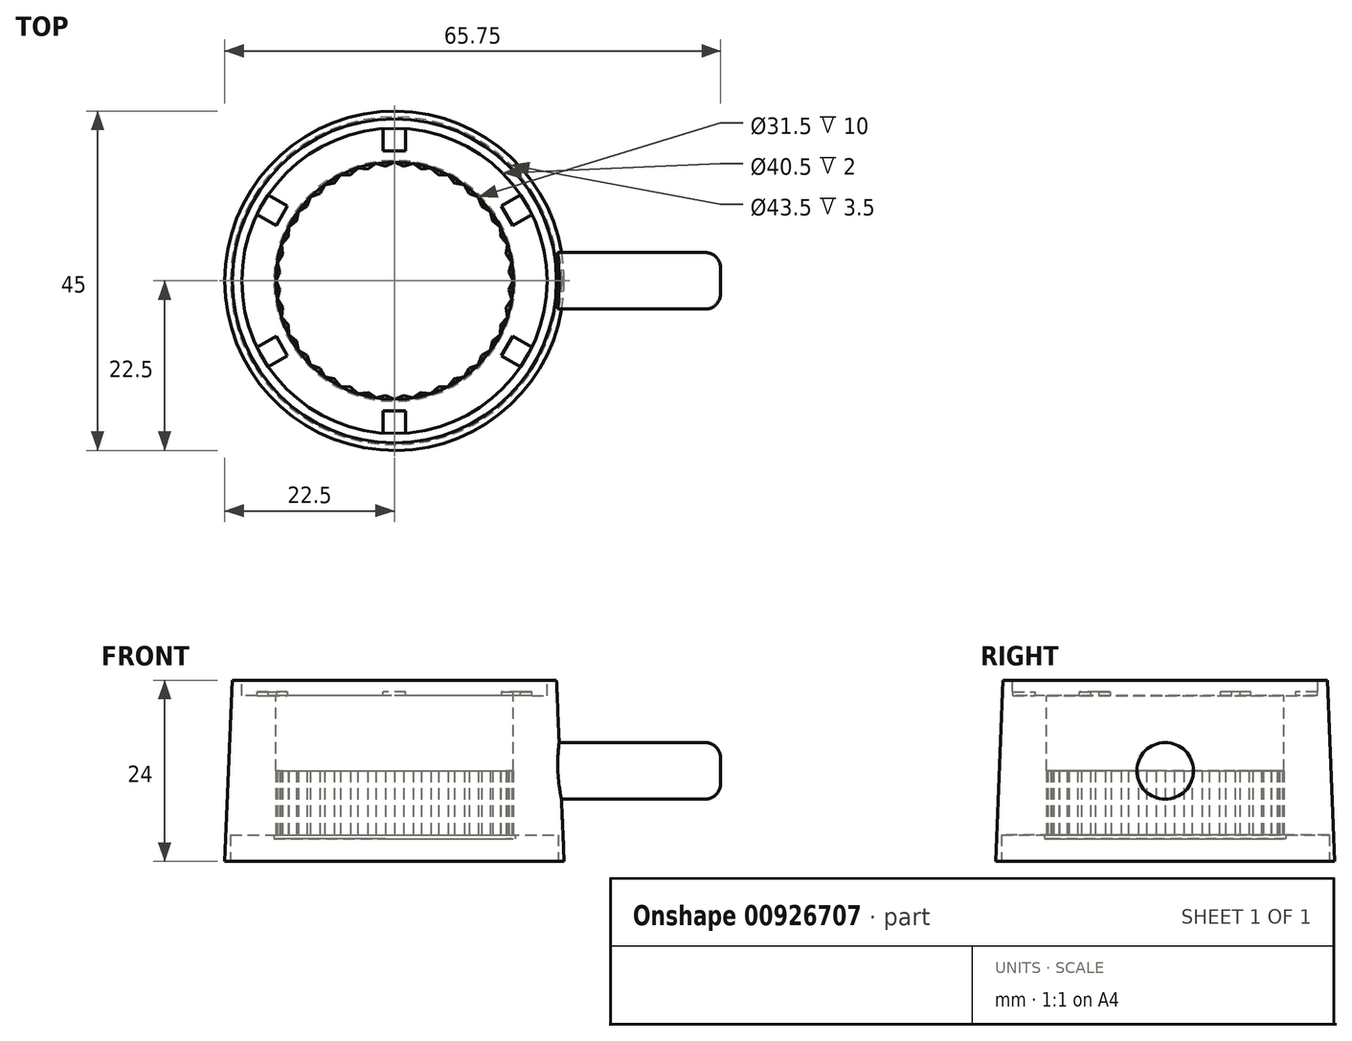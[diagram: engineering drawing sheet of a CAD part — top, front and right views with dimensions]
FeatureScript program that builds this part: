
annotation { "Feature Type Name" : "Feature", "Feature Type Description" : "" }
export const myFeature = defineFeature(function(context is Context, id is Id, definition is map)
    precondition{}
    {
        {
            var Q0;
            Q0=qCreatedBy(makeId("Top.planeOp"),FACE);
            var sketch = newSketch(context, id + "F0", { "sketchPlane" : qUnion([Q0])});
            skCircle(sketch, "E0", {"center": v(0, 0) * mm, "radius": 22.5 * mm});
            skSolve(sketch);
        }
        {
            var Q0;
            Q0=qCreatedBy(makeId("Top.planeOp"),FACE);
            cPlane(context, id + "F1", {"entities" : qUnion([Q0]), "cplaneType" : CPlaneType.OFFSET, "offset" : 24 * mm, "width" : 150 * mm, "height" : 150 * mm});
        }
        {
            var Q0;
            Q0=qCreatedBy(id+"F1.planeOp",FACE);
            var sketch = newSketch(context, id + "F2", { "sketchPlane" : qUnion([Q0])});
            skCircle(sketch, "E1", {"center": v(0, 0) * mm, "radius": 21.5 * mm});
            skSolve(sketch);
        }
        {
            var Q0;
            Q0=makeQuery(id+"F0.imprint","IMPRINT",FACE,{"disambiguationData":[TD([[makeQuery(id+"F0.imprint","IMPRINT",EDGE,{"derivedFrom":sQuery(id+"F0.wireOp",EDGE,"E0")}),1.0]])]});
            var Q1;
            Q1=makeQuery(id+"F2.imprint","IMPRINT",FACE,{"disambiguationData":[TD([[makeQuery(id+"F2.imprint","IMPRINT",EDGE,{"derivedFrom":sQuery(id+"F2.wireOp",EDGE,"E1")}),1.0]])]});
            loft(context, id + "F3", {"sheetProfilesArray" : [{ "sheetProfileEntities" : qUnion([Q0]) }, { "sheetProfileEntities" : qUnion([Q1]) }]});
        }
        {
            var Q0;
            Q0=makeQuery(id+"F3.opLoft","CAP_FACE",FACE,{"disambiguationData":[OSD([makeQuery(id+"F2.imprint","IMPRINT",FACE,{"disambiguationData":[TD([[makeQuery(id+"F2.imprint","IMPRINT",EDGE,{"derivedFrom":sQuery(id+"F2.wireOp",EDGE,"E1")}),1.0]])]})])],"isStart":true});
            var sketch = newSketch(context, id + "F4", { "sketchPlane" : qUnion([Q0])});
            skCircle(sketch, "E2", {"center": v(0, 0) * mm, "radius": 20.25 * mm});
            skSolve(sketch);
        }
        {
            var Q0;
            Q0 = qSketchRegion(id + "F4", true);
            extrude(context, id + "F5", {"entities" : qUnion([Q0]), "operationType" : NewBodyOperationType.REMOVE, "oppositeDirection" : true, "depth" : 2 * mm, "offsetDistance" : 25 * mm});
        }
        {
            var Q0;
            Q0=makeQuery(id+"F3.opLoft","CAP_FACE",FACE,{"disambiguationData":[OSD([makeQuery(id+"F0.imprint","IMPRINT",FACE,{"disambiguationData":[TD([[makeQuery(id+"F0.imprint","IMPRINT",EDGE,{"derivedFrom":sQuery(id+"F0.wireOp",EDGE,"E0")}),1.0]])]})])],"isStart":true});
            var sketch = newSketch(context, id + "F6", { "sketchPlane" : qUnion([Q0])});
            skCircle(sketch, "E3", {"center": v(0, 0) * mm, "radius": 21.75 * mm});
            skSolve(sketch);
        }
        {
            var Q0;
            Q0 = qSketchRegion(id + "F6", true);
            extrude(context, id + "F7", {"entities" : qUnion([Q0]), "operationType" : NewBodyOperationType.REMOVE, "oppositeDirection" : true, "depth" : 3.5 * mm, "offsetDistance" : 25 * mm});
        }
        {
            var Q0;
            Q0=makeQuery(id+"F5.boolean.opBoolean","COPY",FACE,{"derivedFrom":makeQuery(id+"F5.opExtrude","CAP_FACE",FACE,{"disambiguationData":[OSD([sQuery(id+"F4.wireOp",EDGE,"E2")])],"isStart":false})});
            var sketch = newSketch(context, id + "F8", { "sketchPlane" : qUnion([Q0])});
            skCircle(sketch, "E4", {"center": v(0, 0) * mm, "radius": 15.75 * mm});
            skSolve(sketch);
        }
        {
            var Q0;
            Q0 = qSketchRegion(id + "F8", true);
            extrude(context, id + "F9", {"entities" : qUnion([Q0]), "operationType" : NewBodyOperationType.REMOVE, "endBound" : BoundingType.UP_TO_NEXT, "oppositeDirection" : true, "depth" : 25 * mm, "offsetDistance" : 25 * mm});
        }
        {
            var Q0;
            Q0=makeQuery(id+"F5.boolean.opBoolean","COPY",FACE,{"derivedFrom":makeQuery(id+"F5.opExtrude","CAP_FACE",FACE,{"disambiguationData":[OSD([sQuery(id+"F4.wireOp",EDGE,"E2")])],"isStart":false})});
            var sketch = newSketch(context, id + "F10", { "sketchPlane" : qUnion([Q0])});
            skLineSegment(sketch, "E5.bottom", {"start": v(1.5, 20.25) * mm, "end": v(-1.5, 20.25) * mm});
            skLineSegment(sketch, "E5.top", {"start": v(1.5, 17.25) * mm, "end": v(-1.5, 17.25) * mm});
            skLineSegment(sketch, "E5.left", {"start": v(1.5, 20.25) * mm, "end": v(1.5, 17.25) * mm});
            skLineSegment(sketch, "E5.right", {"start": v(-1.5, 20.25) * mm, "end": v(-1.5, 17.25) * mm});
            skPoint(sketch, "E5.middle", {"position": v(0, 18.75) * mm});
            skLineSegment(sketch, "E6.1.0", {"start": v(-14.19, 9.92) * mm, "end": v(-15.69, 7.33) * mm});
            skLineSegment(sketch, "E6.1.1", {"start": v(-16.79, 11.42) * mm, "end": v(-18.29, 8.83) * mm});
            skLineSegment(sketch, "E6.1.2", {"start": v(-18.29, 8.83) * mm, "end": v(-15.69, 7.33) * mm});
            skLineSegment(sketch, "E6.1.3", {"start": v(-16.79, 11.42) * mm, "end": v(-14.19, 9.92) * mm});
            skPoint(sketch, "E6.1.4", {"position": v(-16.24, 9.37) * mm});
            skLineSegment(sketch, "E6.2.0", {"start": v(-15.69, -7.33) * mm, "end": v(-14.19, -9.92) * mm});
            skLineSegment(sketch, "E6.2.1", {"start": v(-18.29, -8.83) * mm, "end": v(-16.79, -11.42) * mm});
            skLineSegment(sketch, "E6.2.2", {"start": v(-16.79, -11.42) * mm, "end": v(-14.19, -9.92) * mm});
            skLineSegment(sketch, "E6.2.3", {"start": v(-18.29, -8.83) * mm, "end": v(-15.69, -7.33) * mm});
            skPoint(sketch, "E6.2.4", {"position": v(-16.24, -9.38) * mm});
            skLineSegment(sketch, "E6.3.0", {"start": v(-1.5, -17.25) * mm, "end": v(1.5, -17.25) * mm});
            skLineSegment(sketch, "E6.3.1", {"start": v(-1.5, -20.25) * mm, "end": v(1.5, -20.25) * mm});
            skLineSegment(sketch, "E6.3.2", {"start": v(1.5, -20.25) * mm, "end": v(1.5, -17.25) * mm});
            skLineSegment(sketch, "E6.3.3", {"start": v(-1.5, -20.25) * mm, "end": v(-1.5, -17.25) * mm});
            skPoint(sketch, "E6.3.4", {"position": v(0, -18.75) * mm});
            skLineSegment(sketch, "E6.4.0", {"start": v(14.19, -9.92) * mm, "end": v(15.69, -7.33) * mm});
            skLineSegment(sketch, "E6.4.1", {"start": v(16.79, -11.42) * mm, "end": v(18.29, -8.83) * mm});
            skLineSegment(sketch, "E6.4.2", {"start": v(18.29, -8.83) * mm, "end": v(15.69, -7.33) * mm});
            skLineSegment(sketch, "E6.4.3", {"start": v(16.79, -11.42) * mm, "end": v(14.19, -9.92) * mm});
            skPoint(sketch, "E6.4.4", {"position": v(16.24, -9.38) * mm});
            skLineSegment(sketch, "E6.5.0", {"start": v(15.69, 7.33) * mm, "end": v(14.19, 9.92) * mm});
            skLineSegment(sketch, "E6.5.1", {"start": v(18.29, 8.83) * mm, "end": v(16.79, 11.42) * mm});
            skLineSegment(sketch, "E6.5.2", {"start": v(16.79, 11.42) * mm, "end": v(14.19, 9.92) * mm});
            skLineSegment(sketch, "E6.5.3", {"start": v(18.29, 8.83) * mm, "end": v(15.69, 7.33) * mm});
            skPoint(sketch, "E6.5.4", {"position": v(16.24, 9.38) * mm});
            skPoint(sketch, "E6.center", {"position": v(0, 0) * mm});
            skSolve(sketch);
        }
        {
            var Q0;
            Q0 = qSketchRegion(id + "F10", true);
            extrude(context, id + "F11", {"entities" : qUnion([Q0]), "operationType" : NewBodyOperationType.ADD, "depth" : 0.5 * mm, "offsetDistance" : 25 * mm});
        }
        {
            var Q0;
            Q0=makeQuery(id+"F7.boolean.opBoolean","COPY",FACE,{"derivedFrom":makeQuery(id+"F7.opExtrude","CAP_FACE",FACE,{"disambiguationData":[OSD([sQuery(id+"F6.wireOp",EDGE,"E3")])],"isStart":false})});
            var sketch = newSketch(context, id + "F12", { "sketchPlane" : qUnion([Q0])});
            skCircle(sketch, "E7.cCircle", {"center": v(0, 0) * mm, "radius": 15.75 * mm, "construction": true});
            skLineSegment(sketch, "E7.0", {"start": v(0, 15.75) * mm, "end": v(4.87, 14.98) * mm});
            skLineSegment(sketch, "E7.1", {"start": v(4.87, 14.98) * mm, "end": v(9.26, 12.74) * mm});
            skLineSegment(sketch, "E7.2", {"start": v(9.26, 12.74) * mm, "end": v(12.74, 9.26) * mm});
            skLineSegment(sketch, "E7.3", {"start": v(12.74, 9.26) * mm, "end": v(14.98, 4.87) * mm});
            skLineSegment(sketch, "E7.4", {"start": v(14.98, 4.87) * mm, "end": v(15.75, 0) * mm});
            skLineSegment(sketch, "E7.5", {"start": v(15.75, 0) * mm, "end": v(14.98, -4.87) * mm});
            skLineSegment(sketch, "E7.6", {"start": v(14.98, -4.87) * mm, "end": v(12.74, -9.26) * mm});
            skLineSegment(sketch, "E7.7", {"start": v(12.74, -9.26) * mm, "end": v(9.26, -12.74) * mm});
            skLineSegment(sketch, "E7.8", {"start": v(9.26, -12.74) * mm, "end": v(4.87, -14.98) * mm});
            skLineSegment(sketch, "E7.9", {"start": v(4.87, -14.98) * mm, "end": v(0, -15.75) * mm});
            skLineSegment(sketch, "E7.10", {"start": v(0, -15.75) * mm, "end": v(-4.87, -14.98) * mm});
            skLineSegment(sketch, "E7.11", {"start": v(-4.87, -14.98) * mm, "end": v(-9.26, -12.74) * mm});
            skLineSegment(sketch, "E7.12", {"start": v(-9.26, -12.74) * mm, "end": v(-12.74, -9.26) * mm});
            skLineSegment(sketch, "E7.13", {"start": v(-12.74, -9.26) * mm, "end": v(-14.98, -4.87) * mm});
            skLineSegment(sketch, "E7.14", {"start": v(-14.98, -4.87) * mm, "end": v(-15.75, 0) * mm});
            skLineSegment(sketch, "E7.15", {"start": v(-15.75, 0) * mm, "end": v(-14.98, 4.87) * mm});
            skLineSegment(sketch, "E7.16", {"start": v(-14.98, 4.87) * mm, "end": v(-12.74, 9.26) * mm});
            skLineSegment(sketch, "E7.17", {"start": v(-12.74, 9.26) * mm, "end": v(-9.26, 12.74) * mm});
            skLineSegment(sketch, "E7.18", {"start": v(-9.26, 12.74) * mm, "end": v(-4.87, 14.98) * mm});
            skLineSegment(sketch, "E7.19", {"start": v(-4.87, 14.98) * mm, "end": v(0, 15.75) * mm});
            skLineSegment(sketch, "E8.1.0", {"start": v(-7.15, -14.03) * mm, "end": v(-11.14, -11.14) * mm});
            skLineSegment(sketch, "E8.1.1", {"start": v(-7.15, 14.03) * mm, "end": v(-2.46, 15.56) * mm});
            skLineSegment(sketch, "E8.1.2", {"start": v(7.15, -14.03) * mm, "end": v(2.46, -15.56) * mm});
            skLineSegment(sketch, "E8.1.3", {"start": v(-15.56, 2.46) * mm, "end": v(-14.03, 7.15) * mm});
            skLineSegment(sketch, "E8.1.4", {"start": v(-14.03, 7.15) * mm, "end": v(-11.14, 11.14) * mm});
            skLineSegment(sketch, "E8.1.5", {"start": v(-2.46, 15.56) * mm, "end": v(2.46, 15.56) * mm});
            skLineSegment(sketch, "E8.1.6", {"start": v(14.03, -7.15) * mm, "end": v(11.14, -11.14) * mm});
            skLineSegment(sketch, "E8.1.7", {"start": v(15.56, -2.46) * mm, "end": v(14.03, -7.15) * mm});
            skLineSegment(sketch, "E8.1.9", {"start": v(14.03, 7.15) * mm, "end": v(15.56, 2.46) * mm});
            skLineSegment(sketch, "E8.1.10", {"start": v(-15.56, -2.46) * mm, "end": v(-15.56, 2.46) * mm});
            skLineSegment(sketch, "E8.1.11", {"start": v(2.46, 15.56) * mm, "end": v(7.15, 14.03) * mm});
            skLineSegment(sketch, "E8.1.12", {"start": v(15.56, 2.46) * mm, "end": v(15.56, -2.46) * mm});
            skLineSegment(sketch, "E8.1.13", {"start": v(7.15, 14.03) * mm, "end": v(11.14, 11.14) * mm});
            skLineSegment(sketch, "E8.1.14", {"start": v(2.46, -15.56) * mm, "end": v(-2.46, -15.56) * mm});
            skLineSegment(sketch, "E8.1.15", {"start": v(-2.46, -15.56) * mm, "end": v(-7.15, -14.03) * mm});
            skLineSegment(sketch, "E8.1.16", {"start": v(-14.03, -7.15) * mm, "end": v(-15.56, -2.46) * mm});
            skLineSegment(sketch, "E8.1.17", {"start": v(-11.14, 11.14) * mm, "end": v(-7.15, 14.03) * mm});
            skLineSegment(sketch, "E8.1.18", {"start": v(11.14, 11.14) * mm, "end": v(14.03, 7.15) * mm});
            skLineSegment(sketch, "E8.1.19", {"start": v(-11.14, -11.14) * mm, "end": v(-14.03, -7.15) * mm});
            skLineSegment(sketch, "E8.1.20", {"start": v(11.14, -11.14) * mm, "end": v(7.15, -14.03) * mm});
            skLineSegment(sketch, "E8.anchor1", {"start": v(0, 0) * mm, "end": v(-9.26, -12.74) * mm, "construction": true});
            skLineSegment(sketch, "E8.anchor2", {"start": v(0, 0) * mm, "end": v(-11.14, -11.14) * mm, "construction": true});
            skSolve(sketch);
        }
        {
            var Q0;
            Q0=makeQuery(id+"F12.imprint","IMPRINT",FACE,{"disambiguationData":[TD([[makeQuery(id+"F12.imprint","IMPRINT",EDGE,{"derivedFrom":makeQuery(id+"F7.boolean.opBoolean","COPY",EDGE,{"derivedFrom":makeQuery(id+"F7.opExtrude","CAP_EDGE",EDGE,{"disambiguationData":[OSD([sQuery(id+"F6.wireOp",EDGE,"E3")])],"isStart":false})})}),1.0]])]});
            var sketch = newSketch(context, id + "F13", { "sketchPlane" : qUnion([Q0])});
            skCircle(sketch, "E9.cCircle", {"center": v(0, 0) * mm, "radius": 15.25 * mm, "construction": true});
            skLineSegment(sketch, "E9.0", {"start": v(1.2, 15.2) * mm, "end": v(5.84, 14.09) * mm});
            skLineSegment(sketch, "E9.1", {"start": v(5.84, 14.09) * mm, "end": v(9.9, 11.6) * mm});
            skLineSegment(sketch, "E9.2", {"start": v(9.9, 11.6) * mm, "end": v(13, 7.97) * mm});
            skLineSegment(sketch, "E9.3", {"start": v(13, 7.97) * mm, "end": v(14.83, 3.56) * mm});
            skLineSegment(sketch, "E9.4", {"start": v(14.83, 3.56) * mm, "end": v(15.2, -1.2) * mm});
            skLineSegment(sketch, "E9.5", {"start": v(15.2, -1.2) * mm, "end": v(14.09, -5.84) * mm});
            skLineSegment(sketch, "E9.6", {"start": v(14.09, -5.84) * mm, "end": v(11.6, -9.9) * mm});
            skLineSegment(sketch, "E9.7", {"start": v(11.6, -9.9) * mm, "end": v(7.97, -13) * mm});
            skLineSegment(sketch, "E9.8", {"start": v(7.97, -13) * mm, "end": v(3.56, -14.83) * mm});
            skLineSegment(sketch, "E9.9", {"start": v(3.56, -14.83) * mm, "end": v(-1.2, -15.2) * mm});
            skLineSegment(sketch, "E9.10", {"start": v(-1.2, -15.2) * mm, "end": v(-5.84, -14.09) * mm});
            skLineSegment(sketch, "E9.11", {"start": v(-5.84, -14.09) * mm, "end": v(-9.9, -11.6) * mm});
            skLineSegment(sketch, "E9.12", {"start": v(-9.9, -11.6) * mm, "end": v(-13, -7.97) * mm});
            skLineSegment(sketch, "E9.13", {"start": v(-13, -7.97) * mm, "end": v(-14.83, -3.56) * mm});
            skLineSegment(sketch, "E9.14", {"start": v(-14.83, -3.56) * mm, "end": v(-15.2, 1.2) * mm});
            skLineSegment(sketch, "E9.15", {"start": v(-15.2, 1.2) * mm, "end": v(-14.09, 5.84) * mm});
            skLineSegment(sketch, "E9.16", {"start": v(-14.09, 5.84) * mm, "end": v(-11.6, 9.9) * mm});
            skLineSegment(sketch, "E9.17", {"start": v(-11.6, 9.9) * mm, "end": v(-7.97, 13) * mm});
            skLineSegment(sketch, "E9.18", {"start": v(-7.97, 13) * mm, "end": v(-3.56, 14.83) * mm});
            skLineSegment(sketch, "E9.19", {"start": v(-3.56, 14.83) * mm, "end": v(1.2, 15.2) * mm});
            skLineSegment(sketch, "E10.1.0", {"start": v(15.2, 1.2) * mm, "end": v(14.83, -3.56) * mm});
            skLineSegment(sketch, "E10.1.1", {"start": v(14.83, -3.56) * mm, "end": v(13, -7.97) * mm});
            skLineSegment(sketch, "E10.1.2", {"start": v(-13, 7.97) * mm, "end": v(-9.9, 11.6) * mm});
            skLineSegment(sketch, "E10.1.3", {"start": v(13, -7.97) * mm, "end": v(9.9, -11.6) * mm});
            skLineSegment(sketch, "E10.1.4", {"start": v(7.97, 13) * mm, "end": v(11.6, 9.9) * mm});
            skLineSegment(sketch, "E10.1.5", {"start": v(-5.84, 14.09) * mm, "end": v(-1.2, 15.2) * mm});
            skLineSegment(sketch, "E10.1.6", {"start": v(-7.97, -13) * mm, "end": v(-11.6, -9.9) * mm});
            skLineSegment(sketch, "E10.1.7", {"start": v(1.2, -15.2) * mm, "end": v(-3.56, -14.83) * mm});
            skLineSegment(sketch, "E10.1.8", {"start": v(11.6, 9.9) * mm, "end": v(14.09, 5.84) * mm});
            skLineSegment(sketch, "E10.1.9", {"start": v(3.56, 14.83) * mm, "end": v(7.97, 13) * mm});
            skLineSegment(sketch, "E10.1.10", {"start": v(9.9, -11.6) * mm, "end": v(5.84, -14.09) * mm});
            skLineSegment(sketch, "E10.1.11", {"start": v(-11.6, -9.9) * mm, "end": v(-14.09, -5.84) * mm});
            skLineSegment(sketch, "E10.1.12", {"start": v(-3.56, -14.83) * mm, "end": v(-7.97, -13) * mm});
            skLineSegment(sketch, "E10.1.13", {"start": v(-9.9, 11.6) * mm, "end": v(-5.84, 14.09) * mm});
            skLineSegment(sketch, "E10.1.15", {"start": v(14.09, 5.84) * mm, "end": v(15.2, 1.2) * mm});
            skLineSegment(sketch, "E10.1.16", {"start": v(-15.2, -1.2) * mm, "end": v(-14.83, 3.56) * mm});
            skLineSegment(sketch, "E10.1.17", {"start": v(5.84, -14.09) * mm, "end": v(1.2, -15.2) * mm});
            skLineSegment(sketch, "E10.1.18", {"start": v(-14.83, 3.56) * mm, "end": v(-13, 7.97) * mm});
            skLineSegment(sketch, "E10.1.19", {"start": v(-1.2, 15.2) * mm, "end": v(3.56, 14.83) * mm});
            skLineSegment(sketch, "E10.1.20", {"start": v(-14.09, -5.84) * mm, "end": v(-15.2, -1.2) * mm});
            skLineSegment(sketch, "E10.anchor1", {"start": v(0, 0) * mm, "end": v(-9.9, -11.6) * mm, "construction": true});
            skLineSegment(sketch, "E10.anchor2", {"start": v(0, 0) * mm, "end": v(-11.6, -9.9) * mm, "construction": true});
            skSolve(sketch);
        }
        {
            var Q0;
            {var subQ0=sQuery(id+"F13.wireOp",EDGE,"E9.19");var subQ1=sQuery(id+"F13.wireOp",EDGE,"E9.0");var subQ2=makeQuery(id+"F13.imprint","INTERSECT",VERTEX,{"derivedFrom":[subQ1,subQ0]});Q0=makeQuery(id+"F13.imprint","IMPRINT",FACE,{"disambiguationData":[TD([[makeQuery(id+"F13.imprint","IMPRINT",EDGE,{"disambiguationData":[TD([[subQ2,-1.0]])],"derivedFrom":subQ1}),-1.0]])]});}
            var sketch = newSketch(context, id + "F14", { "sketchPlane" : qUnion([Q0])});
            skLineSegment(sketch, "E11", {"start": v(0, 15.75) * mm, "end": v(1.2, 15.2) * mm});
            skLineSegment(sketch, "E12", {"start": v(1.2, 15.2) * mm, "end": v(2.46, 15.56) * mm});
            skLineSegment(sketch, "E13.1.0", {"start": v(-1.2, 15.2) * mm, "end": v(0, 15.75) * mm});
            skLineSegment(sketch, "E13.1.1", {"start": v(-2.46, 15.56) * mm, "end": v(-1.2, 15.2) * mm});
            skLineSegment(sketch, "E13.2.0", {"start": v(-3.56, 14.83) * mm, "end": v(-2.46, 15.56) * mm});
            skLineSegment(sketch, "E13.2.1", {"start": v(-4.87, 14.98) * mm, "end": v(-3.56, 14.83) * mm});
            skLineSegment(sketch, "E13.3.0", {"start": v(-5.84, 14.09) * mm, "end": v(-4.87, 14.98) * mm});
            skLineSegment(sketch, "E13.3.1", {"start": v(-7.15, 14.03) * mm, "end": v(-5.84, 14.09) * mm});
            skLineSegment(sketch, "E13.4.0", {"start": v(-7.97, 13) * mm, "end": v(-7.15, 14.03) * mm});
            skLineSegment(sketch, "E13.4.1", {"start": v(-9.26, 12.74) * mm, "end": v(-7.97, 13) * mm});
            skLineSegment(sketch, "E13.5.0", {"start": v(-9.9, 11.6) * mm, "end": v(-9.26, 12.74) * mm});
            skLineSegment(sketch, "E13.5.1", {"start": v(-11.14, 11.14) * mm, "end": v(-9.9, 11.6) * mm});
            skLineSegment(sketch, "E13.6.0", {"start": v(-11.6, 9.9) * mm, "end": v(-11.14, 11.14) * mm});
            skLineSegment(sketch, "E13.6.1", {"start": v(-12.74, 9.26) * mm, "end": v(-11.6, 9.9) * mm});
            skLineSegment(sketch, "E13.7.0", {"start": v(-13, 7.97) * mm, "end": v(-12.74, 9.26) * mm});
            skLineSegment(sketch, "E13.7.1", {"start": v(-14.03, 7.15) * mm, "end": v(-13, 7.97) * mm});
            skLineSegment(sketch, "E13.8.0", {"start": v(-14.09, 5.84) * mm, "end": v(-14.03, 7.15) * mm});
            skLineSegment(sketch, "E13.8.1", {"start": v(-14.98, 4.87) * mm, "end": v(-14.09, 5.84) * mm});
            skLineSegment(sketch, "E13.9.0", {"start": v(-14.83, 3.56) * mm, "end": v(-14.98, 4.87) * mm});
            skLineSegment(sketch, "E13.9.1", {"start": v(-15.56, 2.46) * mm, "end": v(-14.83, 3.56) * mm});
            skLineSegment(sketch, "E13.10.0", {"start": v(-15.2, 1.2) * mm, "end": v(-15.56, 2.46) * mm});
            skLineSegment(sketch, "E13.10.1", {"start": v(-15.75, 0) * mm, "end": v(-15.2, 1.2) * mm});
            skLineSegment(sketch, "E13.11.0", {"start": v(-15.2, -1.2) * mm, "end": v(-15.75, 0) * mm});
            skLineSegment(sketch, "E13.11.1", {"start": v(-15.56, -2.46) * mm, "end": v(-15.2, -1.2) * mm});
            skLineSegment(sketch, "E13.12.0", {"start": v(-14.83, -3.56) * mm, "end": v(-15.56, -2.46) * mm});
            skLineSegment(sketch, "E13.12.1", {"start": v(-14.98, -4.87) * mm, "end": v(-14.83, -3.56) * mm});
            skLineSegment(sketch, "E13.13.0", {"start": v(-14.09, -5.84) * mm, "end": v(-14.98, -4.87) * mm});
            skLineSegment(sketch, "E13.13.1", {"start": v(-14.03, -7.15) * mm, "end": v(-14.09, -5.84) * mm});
            skLineSegment(sketch, "E13.14.0", {"start": v(-13, -7.97) * mm, "end": v(-14.03, -7.15) * mm});
            skLineSegment(sketch, "E13.14.1", {"start": v(-12.74, -9.26) * mm, "end": v(-13, -7.97) * mm});
            skLineSegment(sketch, "E13.15.0", {"start": v(-11.6, -9.9) * mm, "end": v(-12.74, -9.26) * mm});
            skLineSegment(sketch, "E13.15.1", {"start": v(-11.14, -11.14) * mm, "end": v(-11.6, -9.9) * mm});
            skLineSegment(sketch, "E13.16.0", {"start": v(-9.9, -11.6) * mm, "end": v(-11.14, -11.14) * mm});
            skLineSegment(sketch, "E13.16.1", {"start": v(-9.26, -12.74) * mm, "end": v(-9.9, -11.6) * mm});
            skLineSegment(sketch, "E13.17.0", {"start": v(-7.97, -13) * mm, "end": v(-9.26, -12.74) * mm});
            skLineSegment(sketch, "E13.17.1", {"start": v(-7.15, -14.03) * mm, "end": v(-7.97, -13) * mm});
            skLineSegment(sketch, "E13.18.0", {"start": v(-5.84, -14.09) * mm, "end": v(-7.15, -14.03) * mm});
            skLineSegment(sketch, "E13.18.1", {"start": v(-4.87, -14.98) * mm, "end": v(-5.84, -14.09) * mm});
            skLineSegment(sketch, "E13.19.0", {"start": v(-3.56, -14.83) * mm, "end": v(-4.87, -14.98) * mm});
            skLineSegment(sketch, "E13.19.1", {"start": v(-2.46, -15.56) * mm, "end": v(-3.56, -14.83) * mm});
            skLineSegment(sketch, "E13.20.0", {"start": v(-1.2, -15.2) * mm, "end": v(-2.46, -15.56) * mm});
            skLineSegment(sketch, "E13.20.1", {"start": v(0, -15.75) * mm, "end": v(-1.2, -15.2) * mm});
            skLineSegment(sketch, "E13.21.0", {"start": v(1.2, -15.2) * mm, "end": v(0, -15.75) * mm});
            skLineSegment(sketch, "E13.21.1", {"start": v(2.46, -15.56) * mm, "end": v(1.2, -15.2) * mm});
            skLineSegment(sketch, "E13.22.0", {"start": v(3.56, -14.83) * mm, "end": v(2.46, -15.56) * mm});
            skLineSegment(sketch, "E13.22.1", {"start": v(4.87, -14.98) * mm, "end": v(3.56, -14.83) * mm});
            skLineSegment(sketch, "E13.23.0", {"start": v(5.84, -14.09) * mm, "end": v(4.87, -14.98) * mm});
            skLineSegment(sketch, "E13.23.1", {"start": v(7.15, -14.03) * mm, "end": v(5.84, -14.09) * mm});
            skLineSegment(sketch, "E13.24.0", {"start": v(7.97, -13) * mm, "end": v(7.15, -14.03) * mm});
            skLineSegment(sketch, "E13.24.1", {"start": v(9.26, -12.74) * mm, "end": v(7.97, -13) * mm});
            skLineSegment(sketch, "E13.25.0", {"start": v(9.9, -11.6) * mm, "end": v(9.26, -12.74) * mm});
            skLineSegment(sketch, "E13.25.1", {"start": v(11.14, -11.14) * mm, "end": v(9.9, -11.6) * mm});
            skLineSegment(sketch, "E13.26.0", {"start": v(11.6, -9.9) * mm, "end": v(11.14, -11.14) * mm});
            skLineSegment(sketch, "E13.26.1", {"start": v(12.74, -9.26) * mm, "end": v(11.6, -9.9) * mm});
            skLineSegment(sketch, "E13.27.0", {"start": v(13, -7.97) * mm, "end": v(12.74, -9.26) * mm});
            skLineSegment(sketch, "E13.27.1", {"start": v(14.03, -7.15) * mm, "end": v(13, -7.97) * mm});
            skLineSegment(sketch, "E13.28.0", {"start": v(14.09, -5.84) * mm, "end": v(14.03, -7.15) * mm});
            skLineSegment(sketch, "E13.28.1", {"start": v(14.98, -4.87) * mm, "end": v(14.09, -5.84) * mm});
            skLineSegment(sketch, "E13.29.0", {"start": v(14.83, -3.56) * mm, "end": v(14.98, -4.87) * mm});
            skLineSegment(sketch, "E13.29.1", {"start": v(15.56, -2.46) * mm, "end": v(14.83, -3.56) * mm});
            skLineSegment(sketch, "E13.30.0", {"start": v(15.2, -1.2) * mm, "end": v(15.56, -2.46) * mm});
            skLineSegment(sketch, "E13.30.1", {"start": v(15.75, 0) * mm, "end": v(15.2, -1.2) * mm});
            skLineSegment(sketch, "E13.31.0", {"start": v(15.2, 1.2) * mm, "end": v(15.75, 0) * mm});
            skLineSegment(sketch, "E13.31.1", {"start": v(15.56, 2.46) * mm, "end": v(15.2, 1.2) * mm});
            skLineSegment(sketch, "E13.32.0", {"start": v(14.83, 3.56) * mm, "end": v(15.56, 2.46) * mm});
            skLineSegment(sketch, "E13.32.1", {"start": v(14.98, 4.87) * mm, "end": v(14.83, 3.56) * mm});
            skLineSegment(sketch, "E13.33.0", {"start": v(14.09, 5.84) * mm, "end": v(14.98, 4.87) * mm});
            skLineSegment(sketch, "E13.33.1", {"start": v(14.03, 7.15) * mm, "end": v(14.09, 5.84) * mm});
            skLineSegment(sketch, "E13.34.0", {"start": v(13, 7.97) * mm, "end": v(14.03, 7.15) * mm});
            skLineSegment(sketch, "E13.34.1", {"start": v(12.74, 9.26) * mm, "end": v(13, 7.97) * mm});
            skLineSegment(sketch, "E13.35.0", {"start": v(11.6, 9.9) * mm, "end": v(12.74, 9.26) * mm});
            skLineSegment(sketch, "E13.35.1", {"start": v(11.14, 11.14) * mm, "end": v(11.6, 9.9) * mm});
            skLineSegment(sketch, "E13.36.0", {"start": v(9.9, 11.6) * mm, "end": v(11.14, 11.14) * mm});
            skLineSegment(sketch, "E13.36.1", {"start": v(9.26, 12.74) * mm, "end": v(9.9, 11.6) * mm});
            skLineSegment(sketch, "E13.37.0", {"start": v(7.97, 13) * mm, "end": v(9.26, 12.74) * mm});
            skLineSegment(sketch, "E13.37.1", {"start": v(7.15, 14.03) * mm, "end": v(7.97, 13) * mm});
            skLineSegment(sketch, "E13.38.0", {"start": v(5.84, 14.09) * mm, "end": v(7.15, 14.03) * mm});
            skLineSegment(sketch, "E13.38.1", {"start": v(4.87, 14.98) * mm, "end": v(5.84, 14.09) * mm});
            skLineSegment(sketch, "E13.39.0", {"start": v(3.56, 14.83) * mm, "end": v(4.87, 14.98) * mm});
            skLineSegment(sketch, "E13.39.1", {"start": v(2.46, 15.56) * mm, "end": v(3.56, 14.83) * mm});
            skPoint(sketch, "E13.center", {"position": v(0, 0) * mm});
            skCircle(sketch, "E14", {"center": v(0, 0) * mm, "radius": 16 * mm});
            skSolve(sketch);
        }
        {
            var Q0;
            Q0 = qSketchRegion(id + "F14", true);
            extrude(context, id + "F15", {"entities" : qUnion([Q0]), "operationType" : NewBodyOperationType.ADD, "oppositeDirection" : true, "depth" : 8.5 * mm, "offsetDistance" : 25 * mm, "hasSecondDirection" : true, "secondDirectionOppositeDirection" : false, "secondDirectionDepth" : 0.5 * mm});
        }
        {
            var Q0;
            Q0=qCreatedBy(makeId("Right.planeOp"),FACE);
            var Q1;
            Q1=sQuery(id+"F12.wireOp",VERTEX,"E7.4.end");
            cPlane(context, id + "F16", {"entities" : qUnion([Q0, Q1]), "cplaneType" : CPlaneType.PLANE_POINT, "offset" : 25 * mm, "width" : 150 * mm, "height" : 150 * mm});
        }
        {
            var Q0;
            Q0=qCreatedBy(id+"F16.planeOp",FACE);
            cPlane(context, id + "F17", {"entities" : qUnion([Q0]), "cplaneType" : CPlaneType.OFFSET, "offset" : 4.5 * mm, "width" : 150 * mm, "height" : 150 * mm});
        }
        {
            var Q0;
            Q0=qCreatedBy(id+"F17.planeOp",FACE);
            var sketch = newSketch(context, id + "F18", { "sketchPlane" : qUnion([Q0])});
            skCircle(sketch, "E15", {"center": v(0, 12) * mm, "radius": 3.75 * mm});
            skSolve(sketch);
        }
        {
            var Q0;
            Q0 = qSketchRegion(id + "F18", true);
            extrude(context, id + "F19", {"entities" : qUnion([Q0]), "operationType" : NewBodyOperationType.ADD, "depth" : 23 * mm, "offsetDistance" : 25 * mm});
        }
        {
            var Q0;
            Q0=makeQuery(id+"F19.opExtrude","CAP_EDGE",EDGE,{"disambiguationData":[OSD([sQuery(id+"F18.wireOp",EDGE,"E15")])],"isStart":false});
            fillet(context, id + "F20", {"entities" : qUnion([Q0]), "radius" : 2 * mm, "tangentPropagation" : true, "allowEdgeOverflow" : false});
        }
    });
